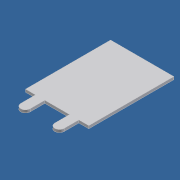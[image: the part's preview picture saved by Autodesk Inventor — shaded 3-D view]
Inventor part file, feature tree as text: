
AUTODESK INVENTOR PART (.ipt)
format: ipt  version: 2014 (Build 180170000, 170)  size: 86,528 bytes
history: native  units: in
note: dims shown in document units (in); Inventor stores cm internally (conversion verified against a paired STEP export)
features: other x7, extrude x1, sketch x1
ambient origin geometry x8: Origin, YZ Plane, XZ Plane, XY Plane, X Axis, Y Axis, Z Axis, Center Point
bodies: Solid1 (feature_tree)
feature tree (9):
  extrude  "Extrusion1"  [1 undecoded]
  other  "shtrmnl_XY"
  other  "shtrmnl_YZ"
  other  "shtrmnl_ZX"
  other  "shtrmnl_X"
  other  "shtrmnl_Y"
  other  "shtrmnl_Z"
  other  "shtrmnl_Center"
  sketch  "Sketch_1"  dims[d0=0.016in d1=0.0in]
note: 1 required parameter value undecoded (feature->parameter linkage not recoverable at this tier; creation-order binding heuristic only, values carry confidence <= 0.55)
